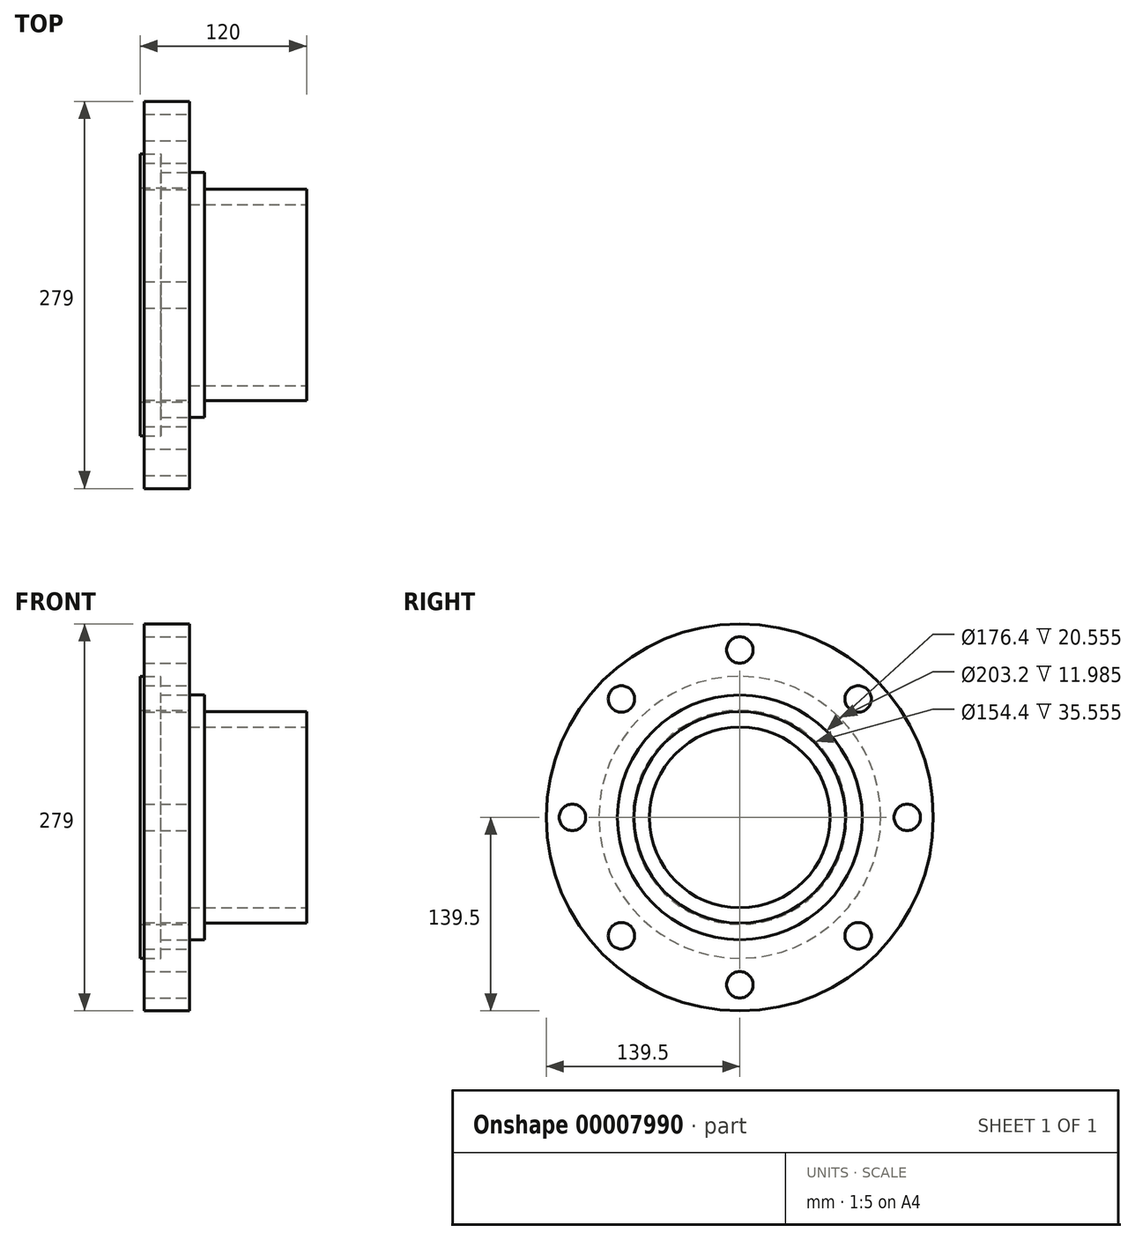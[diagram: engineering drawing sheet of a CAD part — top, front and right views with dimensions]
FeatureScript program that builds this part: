
annotation { "Feature Type Name" : "Feature", "Feature Type Description" : "" }
export const myFeature = defineFeature(function(context is Context, id is Id, definition is map)
    precondition{}
    {
        {
            var Q0;
            Q0=qCreatedBy(makeId("Front.planeOp"),FACE);
            var sketch = newSketch(context, id + "F0", { "sketchPlane" : qUnion([Q0])});
            skLineSegment(sketch, "E0", {"start": v(0, 0) * mm, "end": v(-236.85, 0) * mm, "construction": true});
            skLineSegment(sketch, "E1", {"start": v(-0.07, 101.6) * mm, "end": v(-0.07, 77.2) * mm});
            skLineSegment(sketch, "E2", {"start": v(-0.07, 77.2) * mm, "end": v(35.48, 77.2) * mm});
            skLineSegment(sketch, "E3", {"start": v(35.48, 77.2) * mm, "end": v(35.48, 65.2) * mm});
            skLineSegment(sketch, "E4", {"start": v(35.48, 65.2) * mm, "end": v(119.93, 65.2) * mm});
            skLineSegment(sketch, "E5", {"start": v(119.93, 65.2) * mm, "end": v(119.93, 76.2) * mm});
            skLineSegment(sketch, "E6", {"start": v(119.93, 76.2) * mm, "end": v(46.48, 76.2) * mm});
            skLineSegment(sketch, "E7", {"start": v(46.48, 76.2) * mm, "end": v(46.48, 88.2) * mm});
            skLineSegment(sketch, "E8", {"start": v(46.48, 88.2) * mm, "end": v(14.93, 88.2) * mm});
            skLineSegment(sketch, "E9", {"start": v(14.93, 88.2) * mm, "end": v(14.93, 101.6) * mm});
            skLineSegment(sketch, "E10", {"start": v(-0.07, 101.6) * mm, "end": v(14.93, 101.6) * mm});
            skLineSegment(sketch, "E11", {"start": v(2.94, 101.6) * mm, "end": v(2.94, 139.5) * mm});
            skLineSegment(sketch, "E12", {"start": v(2.94, 139.5) * mm, "end": v(35.48, 139.5) * mm});
            skLineSegment(sketch, "E13", {"start": v(35.48, 139.5) * mm, "end": v(35.48, 88.2) * mm});
            skLineSegment(sketch, "E14", {"start": v(35.48, 88.2) * mm, "end": v(14.93, 88.2) * mm});
            skLineSegment(sketch, "E15", {"start": v(14.93, 101.6) * mm, "end": v(2.94, 101.6) * mm});
            skSolve(sketch);
        }
        {
            var Q0;
            Q0=makeQuery(id+"F0.imprint","IMPRINT",FACE,{"disambiguationData":[TD([[makeQuery(id+"F0.imprint","IMPRINT",EDGE,{"derivedFrom":sQuery(id+"F0.wireOp",EDGE,"E1")}),1.0]])]});
            var Q1;
            Q1=sQuery(id+"F0.wireOp",EDGE,"E0");
            revolve(context, id + "F1", {"entities" : qUnion([Q0]), "axis" : qUnion([Q1]), "revolveType" : RevolveType.FULL});
        }
        {
            var Q0;
            Q0=makeQuery(id+"F0.imprint","IMPRINT",FACE,{"disambiguationData":[TD([[makeQuery(id+"F0.imprint","IMPRINT",EDGE,{"derivedFrom":sQuery(id+"F0.wireOp",EDGE,"E9")}),-1.0]])]});
            var Q1;
            Q1=sQuery(id+"F0.wireOp",EDGE,"E0");
            revolve(context, id + "F2", {"entities" : qUnion([Q0]), "axis" : qUnion([Q1]), "revolveType" : RevolveType.FULL});
        }
        {
            var Q0;
            Q0=makeQuery(id+"F2.opRevolve","SWEPT_FACE",FACE,{"disambiguationData":[OSD([sQuery(id+"F0.wireOp",EDGE,"E13")])]});
            var sketch = newSketch(context, id + "F3", { "sketchPlane" : qUnion([Q0])});
            skCircle(sketch, "E16", {"center": v(0, 120.65) * mm, "radius": 9.53 * mm});
            skCircle(sketch, "E17.1.0", {"center": v(-85.31, 85.31) * mm, "radius": 9.53 * mm});
            skCircle(sketch, "E17.2.0", {"center": v(-120.65, 0) * mm, "radius": 9.53 * mm});
            skCircle(sketch, "E17.3.0", {"center": v(-85.31, -85.31) * mm, "radius": 9.53 * mm});
            skCircle(sketch, "E17.4.0", {"center": v(0, -120.65) * mm, "radius": 9.53 * mm});
            skCircle(sketch, "E17.5.0", {"center": v(85.31, -85.31) * mm, "radius": 9.53 * mm});
            skCircle(sketch, "E17.6.0", {"center": v(120.65, 0) * mm, "radius": 9.53 * mm});
            skCircle(sketch, "E17.7.0", {"center": v(85.31, 85.31) * mm, "radius": 9.53 * mm});
            skPoint(sketch, "E17.center", {"position": v(0, 0) * mm});
            skSolve(sketch);
        }
        {
            var Q0;
            Q0=makeQuery(id+"F3.imprint","IMPRINT",FACE,{"disambiguationData":[TD([[makeQuery(id+"F3.imprint","IMPRINT",EDGE,{"derivedFrom":sQuery(id+"F3.wireOp",EDGE,"E17.1.0")}),1.0]])]});
            var Q1;
            Q1=makeQuery(id+"F3.imprint","IMPRINT",FACE,{"disambiguationData":[TD([[makeQuery(id+"F3.imprint","IMPRINT",EDGE,{"derivedFrom":sQuery(id+"F3.wireOp",EDGE,"E16")}),1.0]])]});
            var Q2;
            Q2=makeQuery(id+"F3.imprint","IMPRINT",FACE,{"disambiguationData":[TD([[makeQuery(id+"F3.imprint","IMPRINT",EDGE,{"derivedFrom":sQuery(id+"F3.wireOp",EDGE,"E17.7.0")}),1.0]])]});
            var Q3;
            Q3=makeQuery(id+"F3.imprint","IMPRINT",FACE,{"disambiguationData":[TD([[makeQuery(id+"F3.imprint","IMPRINT",EDGE,{"derivedFrom":sQuery(id+"F3.wireOp",EDGE,"E17.6.0")}),1.0]])]});
            var Q4;
            Q4=makeQuery(id+"F3.imprint","IMPRINT",FACE,{"disambiguationData":[TD([[makeQuery(id+"F3.imprint","IMPRINT",EDGE,{"derivedFrom":sQuery(id+"F3.wireOp",EDGE,"E17.5.0")}),1.0]])]});
            var Q5;
            Q5=makeQuery(id+"F3.imprint","IMPRINT",FACE,{"disambiguationData":[TD([[makeQuery(id+"F3.imprint","IMPRINT",EDGE,{"derivedFrom":sQuery(id+"F3.wireOp",EDGE,"E17.4.0")}),1.0]])]});
            var Q6;
            Q6=makeQuery(id+"F3.imprint","IMPRINT",FACE,{"disambiguationData":[TD([[makeQuery(id+"F3.imprint","IMPRINT",EDGE,{"derivedFrom":sQuery(id+"F3.wireOp",EDGE,"E17.3.0")}),1.0]])]});
            var Q7;
            Q7=makeQuery(id+"F3.imprint","IMPRINT",FACE,{"disambiguationData":[TD([[makeQuery(id+"F3.imprint","IMPRINT",EDGE,{"derivedFrom":sQuery(id+"F3.wireOp",EDGE,"E17.2.0")}),1.0]])]});
            var Q8;
            Q8=makeQuery(id+"F2.opRevolve","SWEPT_FACE",FACE,{"disambiguationData":[OSD([sQuery(id+"F0.wireOp",EDGE,"E13")])]});
            extrude(context, id + "F4", {"entities" : qUnion([Q0, Q1, Q2, Q3, Q4, Q5, Q6, Q7]), "operationType" : NewBodyOperationType.REMOVE, "endBound" : BoundingType.UP_TO_BODY, "oppositeDirection" : true, "endBoundEntityBody" : qUnion([Q8]), "depth" : 25 * mm});
        }
    });
